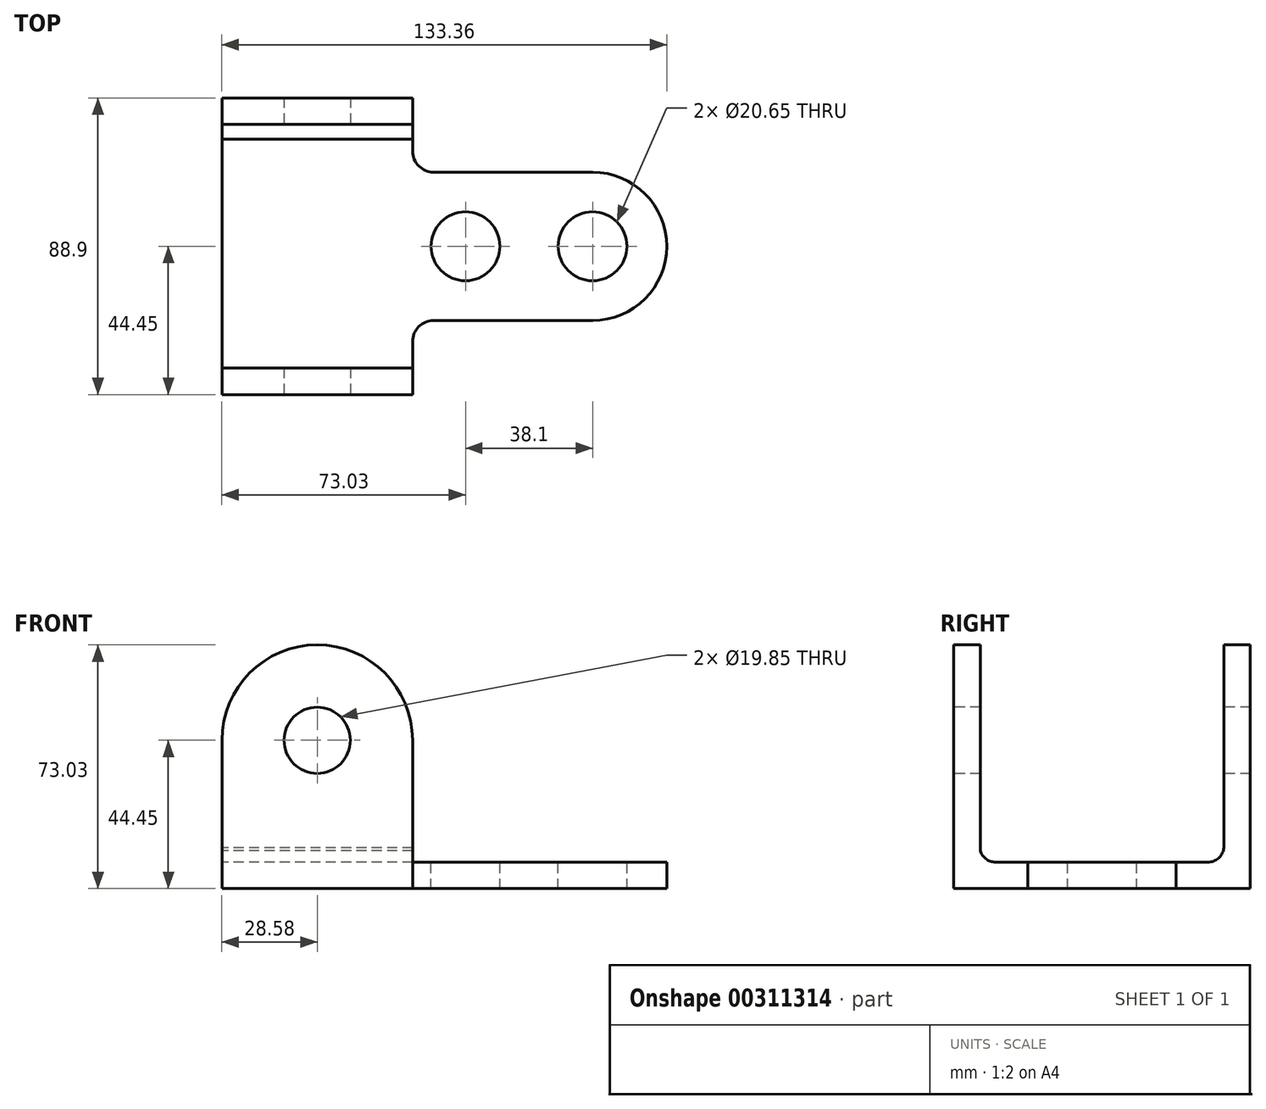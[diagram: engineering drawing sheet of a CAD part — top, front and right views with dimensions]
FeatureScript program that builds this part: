
annotation { "Feature Type Name" : "Feature", "Feature Type Description" : "" }
export const myFeature = defineFeature(function(context is Context, id is Id, definition is map)
    precondition{}
    {
        {
            var Q0;
            Q0=qCreatedBy(makeId("Top.planeOp"),FACE);
            var sketch = newSketch(context, id + "F0", { "sketchPlane" : qUnion([Q0])});
            skArc(sketch, "E0", {"start": v(38.1, -22.23) * mm, "mid": v(60.33, 0) * mm, "end": v(38.1, 22.23) * mm});
            skLineSegment(sketch, "E1", {"start": v(38.1, 22.22) * mm, "end": v(-9.53, 22.22) * mm});
            skLineSegment(sketch, "E2", {"start": v(38.1, -22.23) * mm, "end": v(-9.52, -22.23) * mm});
            skArc(sketch, "E3", {"start": v(-9.53, 22.22) * mm, "mid": v(-14.02, 24.08) * mm, "end": v(-15.88, 28.57) * mm});
            skArc(sketch, "E4", {"start": v(-9.52, -22.23) * mm, "mid": v(-14.02, -24.08) * mm, "end": v(-15.88, -28.58) * mm});
            skLineSegment(sketch, "E5", {"start": v(-15.88, 28.57) * mm, "end": v(-15.88, 44.45) * mm});
            skLineSegment(sketch, "E6", {"start": v(-15.88, 44.45) * mm, "end": v(-73.03, 44.45) * mm});
            skLineSegment(sketch, "E7", {"start": v(-73.03, 44.45) * mm, "end": v(-73.03, -44.45) * mm});
            skLineSegment(sketch, "E8", {"start": v(-73.03, -44.45) * mm, "end": v(-15.88, -44.45) * mm});
            skLineSegment(sketch, "E9", {"start": v(-15.88, -44.45) * mm, "end": v(-15.88, -28.58) * mm});
            skLineSegment(sketch, "E10", {"start": v(-9.53, 22.22) * mm, "end": v(38.1, 22.23) * mm});
            skLineSegment(sketch, "E11", {"start": v(-9.52, -22.23) * mm, "end": v(38.1, -22.23) * mm});
            skPoint(sketch, "E12.center.orphan", {"position": v(0, 0) * mm});
            skSolve(sketch);
        }
        {
            var Q0;
            Q0 = qSketchRegion(id + "F0", true);
            extrude(context, id + "F1", {"entities" : qUnion([Q0]), "depth" : 7.94 * mm});
        }
        {
            var Q0;
            Q0=makeQuery(id+"F1.opExtrude","CAP_FACE",FACE,{"disambiguationData":[OSD([sQuery(id+"F0.wireOp",EDGE,"E0"),sQuery(id+"F0.wireOp",EDGE,"E3"),sQuery(id+"F0.wireOp",EDGE,"E4"),sQuery(id+"F0.wireOp",EDGE,"E5"),sQuery(id+"F0.wireOp",EDGE,"E6"),sQuery(id+"F0.wireOp",EDGE,"E7"),sQuery(id+"F0.wireOp",EDGE,"E8"),sQuery(id+"F0.wireOp",EDGE,"E9"),sQuery(id+"F0.wireOp",EDGE,"E10"),sQuery(id+"F0.wireOp",EDGE,"E11")])],"isStart":false});
            var sketch = newSketch(context, id + "F2", { "sketchPlane" : qUnion([Q0])});
            skLineSegment(sketch, "E13.bottom", {"start": v(-73.03, 44.45) * mm, "end": v(-15.88, 44.45) * mm});
            skLineSegment(sketch, "E13.top", {"start": v(-73.03, 36.51) * mm, "end": v(-15.88, 36.51) * mm});
            skLineSegment(sketch, "E13.left", {"start": v(-73.03, 44.45) * mm, "end": v(-73.03, 36.51) * mm});
            skLineSegment(sketch, "E13.right", {"start": v(-15.88, 44.45) * mm, "end": v(-15.88, 36.51) * mm});
            skLineSegment(sketch, "E14.bottom", {"start": v(-15.88, -44.45) * mm, "end": v(-73.03, -44.45) * mm});
            skLineSegment(sketch, "E14.top", {"start": v(-15.88, -36.51) * mm, "end": v(-73.03, -36.51) * mm});
            skLineSegment(sketch, "E14.left", {"start": v(-15.88, -44.45) * mm, "end": v(-15.88, -36.51) * mm});
            skLineSegment(sketch, "E14.right", {"start": v(-73.03, -44.45) * mm, "end": v(-73.03, -36.51) * mm});
            skSolve(sketch);
        }
        {
            var Q0;
            Q0 = qSketchRegion(id + "F2", true);
            extrude(context, id + "F3", {"entities" : qUnion([Q0]), "operationType" : NewBodyOperationType.ADD, "depth" : 76.2 * mm});
        }
        {
            var Q0;
            Q0=makeQuery(id+"F3.boolean.opBoolean","MERGE",FACE,{"derivedFrom":[makeQuery(id+"F1.opExtrude","SWEPT_FACE",FACE,{"disambiguationData":[OSD([sQuery(id+"F0.wireOp",EDGE,"E8")])]}),makeQuery(id+"F3.opExtrude","SWEPT_FACE",FACE,{"disambiguationData":[OSD([sQuery(id+"F2.wireOp",EDGE,"E14.bottom")])]})]});
            var sketch = newSketch(context, id + "F4", { "sketchPlane" : qUnion([Q0])});
            skLineSegment(sketch, "E15", {"start": v(-44.45, 0) * mm, "end": v(-44.45, 104.1) * mm, "construction": true});
            skLineSegment(sketch, "E16", {"start": v(-89.2, 44.45) * mm, "end": v(-6.37, 44.45) * mm, "construction": true});
            skArc(sketch, "E17", {"start": v(-15.88, 44.45) * mm, "mid": v(-44.45, 73.03) * mm, "end": v(-73.03, 44.45) * mm});
            skLineSegment(sketch, "E18", {"start": v(-73.03, 44.45) * mm, "end": v(-73.03, 84.14) * mm});
            skLineSegment(sketch, "E19", {"start": v(-73.03, 84.14) * mm, "end": v(-15.88, 84.14) * mm});
            skLineSegment(sketch, "E20", {"start": v(-15.88, 84.14) * mm, "end": v(-15.88, 44.45) * mm});
            skCircle(sketch, "E21", {"center": v(-44.45, 44.45) * mm, "radius": 9.92 * mm});
            skSolve(sketch);
        }
        {
            var Q0;
            Q0=makeQuery(id+"F4.imprint","IMPRINT",FACE,{"disambiguationData":[TD([[makeQuery(id+"F4.imprint","IMPRINT",EDGE,{"derivedFrom":sQuery(id+"F4.wireOp",EDGE,"E17")}),-1.0]])]});
            var Q1;
            Q1=makeQuery(id+"F4.imprint","IMPRINT",FACE,{"disambiguationData":[TD([[makeQuery(id+"F4.imprint","IMPRINT",EDGE,{"derivedFrom":sQuery(id+"F4.wireOp",EDGE,"E21")}),1.0]])]});
            extrude(context, id + "F5", {"entities" : qUnion([Q0, Q1]), "operationType" : NewBodyOperationType.REMOVE, "endBound" : BoundingType.THROUGH_ALL, "oppositeDirection" : true, "depth" : 25.4 * mm});
        }
        {
            var Q0;
            Q0=makeQuery(id+"F1.opExtrude","CAP_FACE",FACE,{"disambiguationData":[OSD([sQuery(id+"F0.wireOp",EDGE,"E0"),sQuery(id+"F0.wireOp",EDGE,"E3"),sQuery(id+"F0.wireOp",EDGE,"E4"),sQuery(id+"F0.wireOp",EDGE,"E5"),sQuery(id+"F0.wireOp",EDGE,"E6"),sQuery(id+"F0.wireOp",EDGE,"E7"),sQuery(id+"F0.wireOp",EDGE,"E8"),sQuery(id+"F0.wireOp",EDGE,"E9"),sQuery(id+"F0.wireOp",EDGE,"E10"),sQuery(id+"F0.wireOp",EDGE,"E11")])],"isStart":false});
            var sketch = newSketch(context, id + "F6", { "sketchPlane" : qUnion([Q0])});
            skCircle(sketch, "E22", {"center": v(38.1, 0) * mm, "radius": 10.33 * mm});
            skCircle(sketch, "E23", {"center": v(0, 0) * mm, "radius": 10.33 * mm});
            skSolve(sketch);
        }
        {
            var Q0;
            Q0 = qSketchRegion(id + "F6", true);
            extrude(context, id + "F7", {"entities" : qUnion([Q0]), "operationType" : NewBodyOperationType.REMOVE, "oppositeDirection" : true, "depth" : 25.4 * mm});
        }
        {
            var Q0;
            Q0=makeQuery(id+"F3.boolean.opBoolean","MERGE",FACE,{"derivedFrom":[makeQuery(id+"F1.opExtrude","SWEPT_FACE",FACE,{"disambiguationData":[OSD([sQuery(id+"F0.wireOp",EDGE,"E7")])]}),makeQuery(id+"F3.opExtrude","SWEPT_FACE",FACE,{"disambiguationData":[OSD([sQuery(id+"F2.wireOp",EDGE,"E13.left")])]}),makeQuery(id+"F3.opExtrude","SWEPT_FACE",FACE,{"disambiguationData":[OSD([sQuery(id+"F2.wireOp",EDGE,"E14.right")])]})]});
            var sketch = newSketch(context, id + "F8", { "sketchPlane" : qUnion([Q0])});
            skArc(sketch, "E24", {"start": v(-36.51, 13.08) * mm, "mid": v(-35.14, 9.32) * mm, "end": v(-31.38, 7.94) * mm});
            skArc(sketch, "E25", {"start": v(31.95, 7.94) * mm, "mid": v(35.75, 9.84) * mm, "end": v(36.51, 14.03) * mm});
            skLineSegment(sketch, "E26", {"start": v(-36.51, 13.08) * mm, "end": v(-36.51, 7.94) * mm});
            skLineSegment(sketch, "E27", {"start": v(-36.51, 7.94) * mm, "end": v(-31.38, 7.94) * mm});
            skLineSegment(sketch, "E28", {"start": v(36.51, 14.03) * mm, "end": v(36.51, 7.94) * mm});
            skLineSegment(sketch, "E29", {"start": v(36.51, 7.94) * mm, "end": v(31.95, 7.94) * mm});
            skSolve(sketch);
        }
        {
            var Q0;
            Q0 = qSketchRegion(id + "F8", true);
            extrude(context, id + "F9", {"entities" : qUnion([Q0]), "operationType" : NewBodyOperationType.ADD, "oppositeDirection" : true, "depth" : 57.15 * mm});
        }
    });
